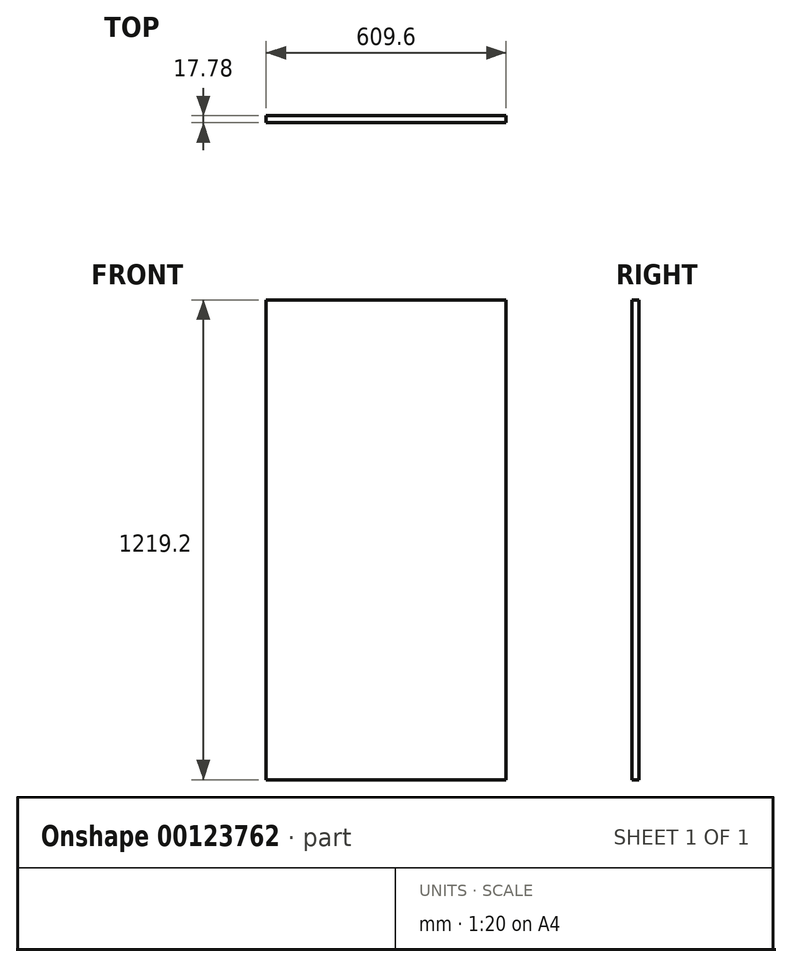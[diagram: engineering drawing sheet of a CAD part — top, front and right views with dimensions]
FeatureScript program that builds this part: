
annotation { "Feature Type Name" : "Feature", "Feature Type Description" : "" }
export const myFeature = defineFeature(function(context is Context, id is Id, definition is map)
    precondition{}
    {
        {
            var Q0;
            Q0=qCreatedBy(makeId("Front.planeOp"),FACE);
            var sketch = newSketch(context, id + "F0", { "sketchPlane" : qUnion([Q0])});
            skLineSegment(sketch, "E0.bottom", {"start": v(-183.93, 1021.05) * mm, "end": v(425.67, 1021.05) * mm});
            skLineSegment(sketch, "E0.top", {"start": v(-183.93, -198.15) * mm, "end": v(425.67, -198.15) * mm});
            skLineSegment(sketch, "E0.left", {"start": v(-183.93, 1021.05) * mm, "end": v(-183.93, -198.15) * mm});
            skLineSegment(sketch, "E0.right", {"start": v(425.67, 1021.05) * mm, "end": v(425.67, -198.15) * mm});
            skSolve(sketch);
        }
        {
            var Q0;
            Q0=makeQuery(id+"F0.imprint","IMPRINT",FACE,{"disambiguationData":[TD([[makeQuery(id+"F0.imprint","IMPRINT",EDGE,{"derivedFrom":sQuery(id+"F0.wireOp",EDGE,"E0.bottom")}),-1.0]])]});
            extrude(context, id + "F1", {"entities" : qUnion([Q0]), "depth" : 17.78 * mm});
        }
    });
